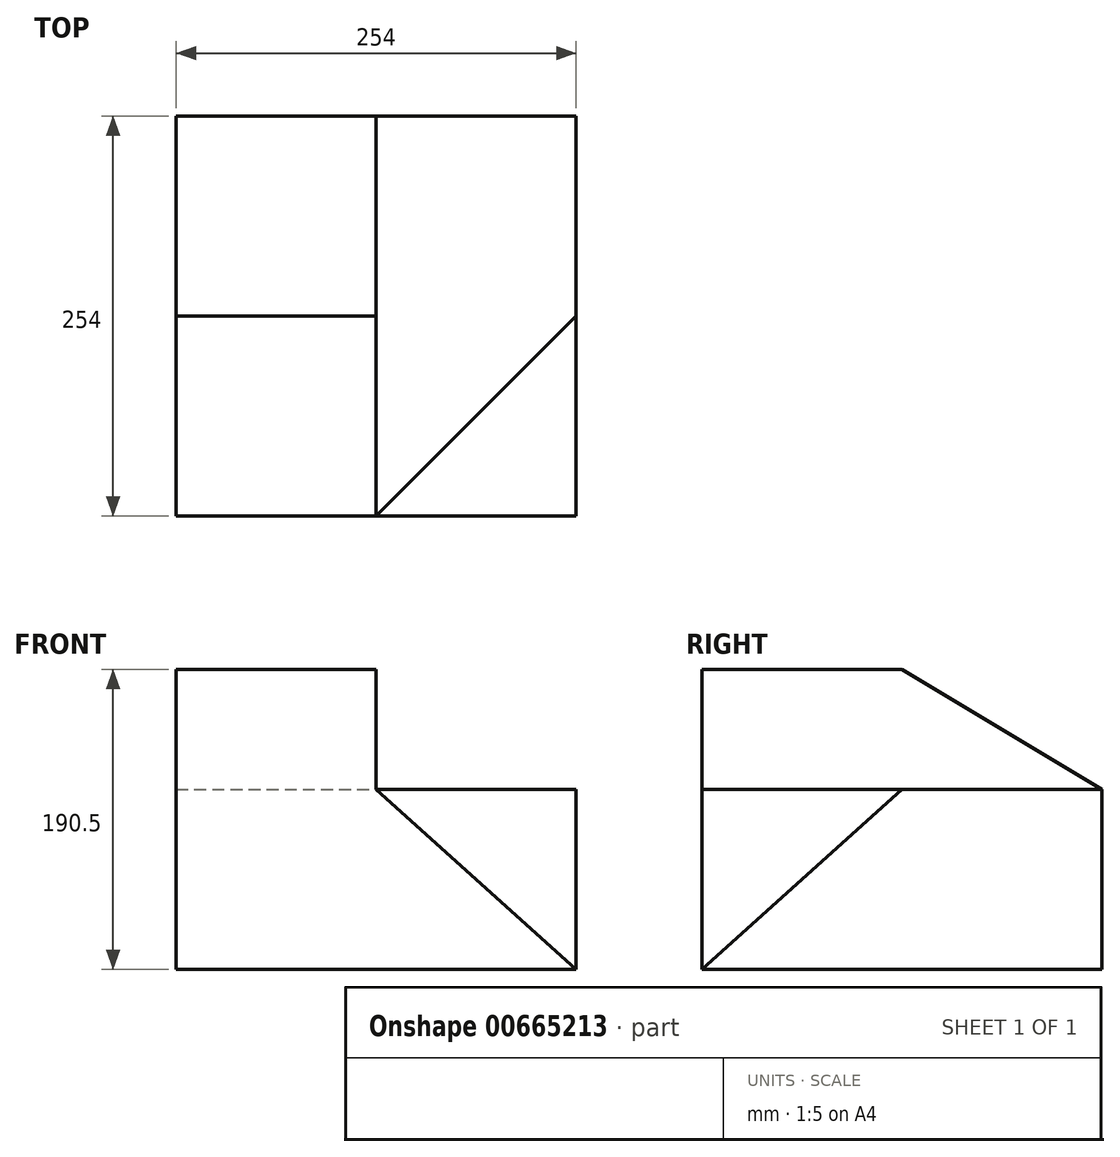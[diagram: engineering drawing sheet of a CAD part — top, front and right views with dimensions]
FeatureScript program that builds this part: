
annotation { "Feature Type Name" : "Feature", "Feature Type Description" : "" }
export const myFeature = defineFeature(function(context is Context, id is Id, definition is map)
    precondition{}
    {
        {
            var Q0;
            Q0=qCreatedBy(makeId("Front.planeOp"),FACE);
            var sketch = newSketch(context, id + "F0", { "sketchPlane" : qUnion([Q0])});
            skLineSegment(sketch, "E0", {"start": v(0, 0) * mm, "end": v(0, 190.5) * mm});
            skLineSegment(sketch, "E1", {"start": v(0, 190.5) * mm, "end": v(127, 190.5) * mm});
            skLineSegment(sketch, "E2", {"start": v(127, 190.5) * mm, "end": v(127, 114.3) * mm});
            skLineSegment(sketch, "E3", {"start": v(127, 114.3) * mm, "end": v(254, 114.3) * mm});
            skLineSegment(sketch, "E4", {"start": v(254, 114.3) * mm, "end": v(254, 0) * mm});
            skLineSegment(sketch, "E5", {"start": v(254, 0) * mm, "end": v(0, 0) * mm});
            skSolve(sketch);
        }
        {
            var Q0;
            Q0=makeQuery(id+"F0.imprint","IMPRINT",FACE,{"disambiguationData":[TD([[makeQuery(id+"F0.imprint","IMPRINT",EDGE,{"derivedFrom":sQuery(id+"F0.wireOp",EDGE,"E0")}),-1.0]])]});
            extrude(context, id + "F1", {"entities" : qUnion([Q0]), "endBound" : BoundingType.SYMMETRIC, "depth" : 254 * mm, "offsetDistance" : 25.4 * mm});
        }
        {
            var Q0;
            Q0=makeQuery(id+"F1.opExtrude","SWEPT_FACE",FACE,{"disambiguationData":[OSD([sQuery(id+"F0.wireOp",EDGE,"E2")])]});
            var sketch = newSketch(context, id + "F2", { "sketchPlane" : qUnion([Q0])});
            skLineSegment(sketch, "E6", {"start": v(0, 190.5) * mm, "end": v(127, 114.3) * mm});
            skLineSegment(sketch, "E7", {"start": v(127, 114.3) * mm, "end": v(127, 190.5) * mm});
            skLineSegment(sketch, "E8", {"start": v(127, 190.5) * mm, "end": v(0, 190.5) * mm});
            skSolve(sketch);
        }
        {
            var Q0;
            Q0=makeQuery(id+"F2.imprint","IMPRINT",FACE,{"disambiguationData":[TD([[makeQuery(id+"F2.imprint","IMPRINT",EDGE,{"derivedFrom":sQuery(id+"F2.wireOp",EDGE,"E6")}),1.0]])]});
            extrude(context, id + "F3", {"entities" : qUnion([Q0]), "operationType" : NewBodyOperationType.REMOVE, "oppositeDirection" : true, "depth" : 254 * mm, "offsetDistance" : 25.4 * mm});
        }
        {
            var Q0;
            Q0=makeQuery(id+"F1.opExtrude","SWEPT_EDGE",EDGE,{"disambiguationData":[OSD([sQuery(id+"F0.wireOp",EDGE,"E3"),sQuery(id+"F0.wireOp",EDGE,"E4")])]});
            cPoint(context, id + "F4", {"entities" : qUnion([Q0]), "parameter" : 0.5});
        }
        {
            var Q0;
            Q0=makeQuery(id+"F1.opExtrude","CAP_VERTEX",VERTEX,{"disambiguationData":[OSD([sQuery(id+"F0.wireOp",EDGE,"E2"),sQuery(id+"F0.wireOp",EDGE,"E3")])],"isStart":false});
            var Q1;
            Q1 = qCreatedBy(id + "F4" ,VERTEX);
            var Q2;
            Q2=makeQuery(id+"F1.opExtrude","CAP_VERTEX",VERTEX,{"disambiguationData":[OSD([sQuery(id+"F0.wireOp",EDGE,"E4"),sQuery(id+"F0.wireOp",EDGE,"E5")])],"isStart":false});
            cPlane(context, id + "F5", {"entities" : qUnion([Q0, Q1, Q2]), "cplaneType" : CPlaneType.THREE_POINT, "offset" : 25.4 * mm, "width" : 152.4 * mm, "height" : 152.4 * mm});
        }
        {
            var Q0;
            Q0=qCreatedBy(id+"F5.planeOp",FACE);
            var sketch = newSketch(context, id + "F6", { "sketchPlane" : qUnion([Q0])});
            skLineSegment(sketch, "E9", {"start": v(163.88, 76.46) * mm, "end": v(11.08, -17.94) * mm});
            skLineSegment(sketch, "E10", {"start": v(163.88, -94.4) * mm, "end": v(163.88, 76.46) * mm});
            skLineSegment(sketch, "E11", {"start": v(11.08, -17.94) * mm, "end": v(163.88, -94.4) * mm});
            skLineSegment(sketch, "E12", {"start": v(-90.78, 33.04) * mm, "end": v(11.08, -17.94) * mm});
            skSolve(sketch);
        }
        {
            var Q0;
            Q0=makeQuery(id+"F6.imprint","IMPRINT",FACE,{"disambiguationData":[TD([[makeQuery(id+"F6.imprint","IMPRINT",EDGE,{"derivedFrom":sQuery(id+"F6.wireOp",EDGE,"E9")}),1.0]])]});
            extrude(context, id + "F7", {"entities" : qUnion([Q0]), "operationType" : NewBodyOperationType.REMOVE, "endBound" : BoundingType.THROUGH_ALL, "depth" : 25.4 * mm, "offsetDistance" : 25.4 * mm});
        }
    });
